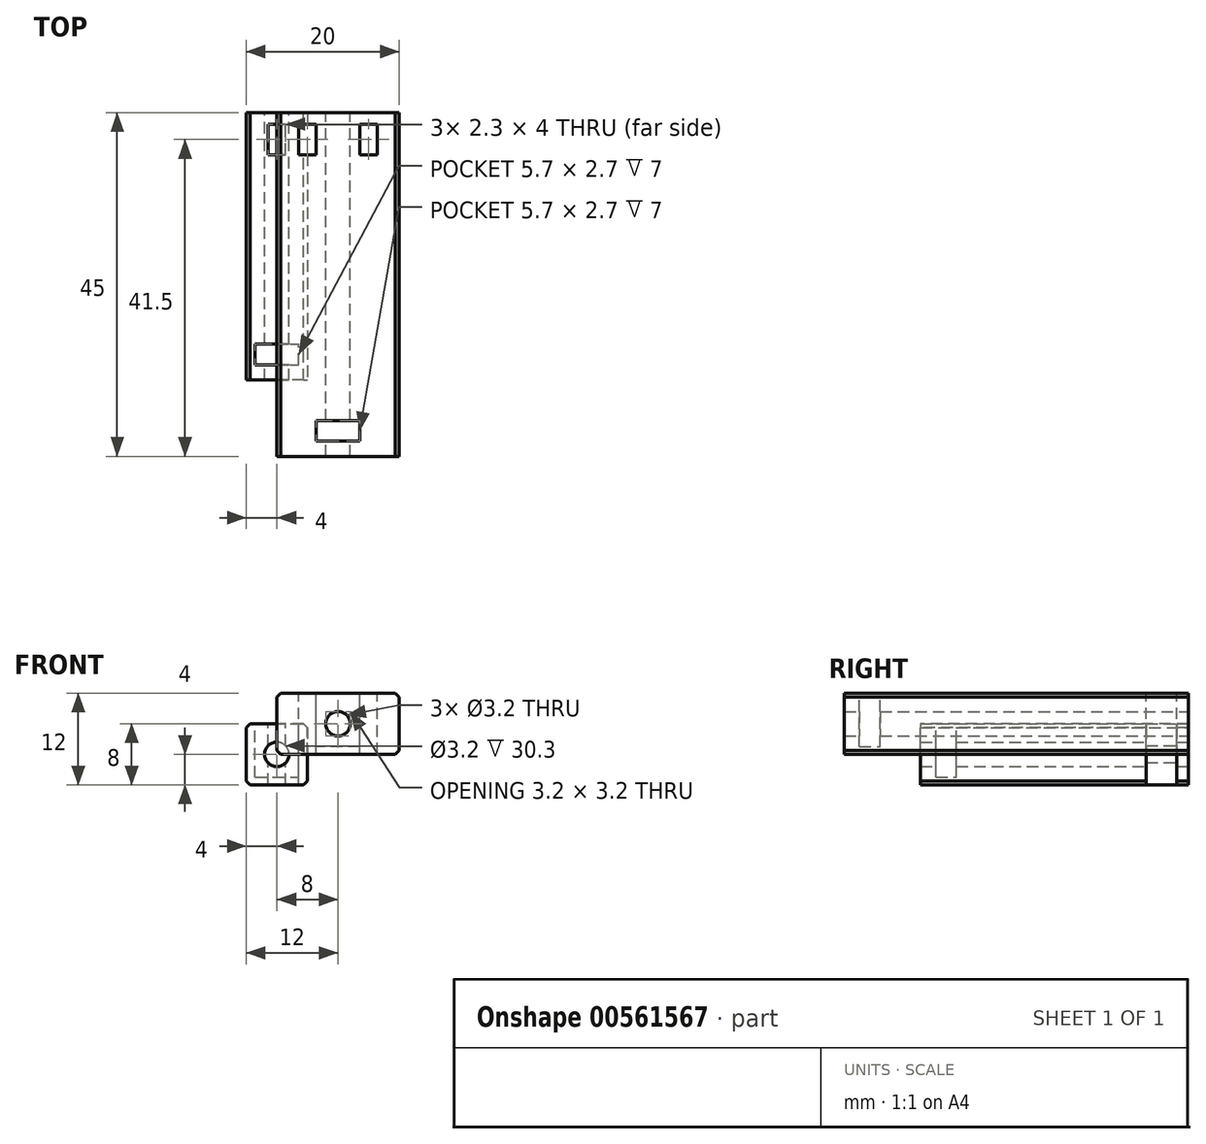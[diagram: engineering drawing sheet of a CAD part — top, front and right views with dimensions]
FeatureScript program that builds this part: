
annotation { "Feature Type Name" : "Feature", "Feature Type Description" : "" }
export const myFeature = defineFeature(function(context is Context, id is Id, definition is map)
    precondition{}
    {
        {
            var Q0;
            Q0=qCreatedBy(makeId("Front.planeOp"),FACE);
            var sketch = newSketch(context, id + "F0", { "sketchPlane" : qUnion([Q0])});
            skLineSegment(sketch, "E0.bottom", {"start": v(4, -4) * mm, "end": v(-4, -4) * mm});
            skLineSegment(sketch, "E0.top", {"start": v(4, 4) * mm, "end": v(-4, 4) * mm});
            skLineSegment(sketch, "E0.left", {"start": v(4, -4) * mm, "end": v(4, 4) * mm});
            skLineSegment(sketch, "E0.right", {"start": v(-4, -4) * mm, "end": v(-4, 4) * mm});
            skPoint(sketch, "E0.middle", {"position": v(0, 0) * mm});
            skCircle(sketch, "E1", {"center": v(0, 0) * mm, "radius": 1.6 * mm});
            skSolve(sketch);
        }
        {
            var Q0;
            Q0=makeQuery(id+"F0.imprint","IMPRINT",FACE,{"disambiguationData":[TD([[makeQuery(id+"F0.imprint","IMPRINT",EDGE,{"derivedFrom":sQuery(id+"F0.wireOp",EDGE,"E0.bottom")}),-1.0]])]});
            extrude(context, id + "F1", {"entities" : qUnion([Q0]), "depth" : 35 * mm});
        }
        {
            var Q0;
            Q0=makeQuery(id+"F1.opExtrude","SWEPT_FACE",FACE,{"disambiguationData":[OSD([sQuery(id+"F0.wireOp",EDGE,"E0.top")])]});
            var sketch = newSketch(context, id + "F2", { "sketchPlane" : qUnion([Q0])});
            skLineSegment(sketch, "E2.bottom", {"start": v(-2.85, -33) * mm, "end": v(2.85, -33) * mm});
            skLineSegment(sketch, "E2.top", {"start": v(-2.85, -30.3) * mm, "end": v(2.85, -30.3) * mm});
            skLineSegment(sketch, "E2.left", {"start": v(-2.85, -33) * mm, "end": v(-2.85, -30.3) * mm});
            skLineSegment(sketch, "E2.right", {"start": v(2.85, -33) * mm, "end": v(2.85, -30.3) * mm});
            skPoint(sketch, "E2.middle", {"position": v(0, -31.65) * mm});
            skSolve(sketch);
        }
        {
            var Q0;
            Q0=makeQuery(id+"F2.imprint","IMPRINT",FACE,{"disambiguationData":[TD([[makeQuery(id+"F2.imprint","IMPRINT",EDGE,{"derivedFrom":sQuery(id+"F2.wireOp",EDGE,"E2.bottom")}),1.0]])]});
            extrude(context, id + "F3", {"entities" : qUnion([Q0]), "operationType" : NewBodyOperationType.REMOVE, "oppositeDirection" : true, "depth" : 7 * mm});
        }
        {
            var Q0;
            Q0=makeQuery(id+"F1.opExtrude","SWEPT_FACE",FACE,{"disambiguationData":[OSD([sQuery(id+"F0.wireOp",EDGE,"E0.top")])]});
            var sketch = newSketch(context, id + "F4", { "sketchPlane" : qUnion([Q0])});
            skLineSegment(sketch, "E3.bottom", {"start": v(-1.15, -5.5) * mm, "end": v(1.15, -5.5) * mm});
            skLineSegment(sketch, "E3.top", {"start": v(-1.15, -1.5) * mm, "end": v(1.15, -1.5) * mm});
            skLineSegment(sketch, "E3.left", {"start": v(-1.15, -5.5) * mm, "end": v(-1.15, -1.5) * mm});
            skLineSegment(sketch, "E3.right", {"start": v(1.15, -5.5) * mm, "end": v(1.15, -1.5) * mm});
            skPoint(sketch, "E3.middle", {"position": v(0, -3.5) * mm});
            skSolve(sketch);
        }
        {
            var Q0;
            Q0=makeQuery(id+"F4.imprint","IMPRINT",FACE,{"disambiguationData":[TD([[makeQuery(id+"F4.imprint","IMPRINT",EDGE,{"derivedFrom":sQuery(id+"F4.wireOp",EDGE,"E3.bottom")}),1.0]])]});
            extrude(context, id + "F5", {"entities" : qUnion([Q0]), "operationType" : NewBodyOperationType.REMOVE, "endBound" : BoundingType.THROUGH_ALL, "oppositeDirection" : true, "depth" : 25 * mm});
        }
        {
            var Q0;
            Q0=makeQuery(id+"F1.opExtrude","SWEPT_EDGE",EDGE,{"disambiguationData":[OSD([sQuery(id+"F0.wireOp",EDGE,"E0.top"),sQuery(id+"F0.wireOp",EDGE,"E0.right")])]});
            var Q1;
            Q1=makeQuery(id+"F1.opExtrude","SWEPT_EDGE",EDGE,{"disambiguationData":[OSD([sQuery(id+"F0.wireOp",EDGE,"E0.top"),sQuery(id+"F0.wireOp",EDGE,"E0.left")])]});
            var Q2;
            Q2=makeQuery(id+"F1.opExtrude","SWEPT_EDGE",EDGE,{"disambiguationData":[OSD([sQuery(id+"F0.wireOp",EDGE,"E0.bottom"),sQuery(id+"F0.wireOp",EDGE,"E0.right")])]});
            var Q3;
            Q3=makeQuery(id+"F1.opExtrude","SWEPT_EDGE",EDGE,{"disambiguationData":[OSD([sQuery(id+"F0.wireOp",EDGE,"E0.bottom"),sQuery(id+"F0.wireOp",EDGE,"E0.left")])]});
            chamfer(context, id + "F6", {"entities" : qUnion([Q0, Q1, Q2, Q3]), "width" : .5 * mm, "tangentPropagation" : true});
        }
        {
            var Q0;
            Q0=qCreatedBy(makeId("Front.planeOp"),FACE);
            var sketch = newSketch(context, id + "F7", { "sketchPlane" : qUnion([Q0])});
            skLineSegment(sketch, "E4.bottom", {"start": v(0, 0) * mm, "end": v(16, 0) * mm});
            skLineSegment(sketch, "E4.top", {"start": v(0, 8) * mm, "end": v(16, 8) * mm});
            skLineSegment(sketch, "E4.left", {"start": v(0, 0) * mm, "end": v(0, 8) * mm});
            skLineSegment(sketch, "E4.right", {"start": v(16, 0) * mm, "end": v(16, 8) * mm});
            skCircle(sketch, "E5", {"center": v(8, 4) * mm, "radius": 1.6 * mm});
            skPoint(sketch, "E5.centerSnap0", {"position": v(8, 8) * mm});
            skLineSegment(sketch, "E6", {"start": v(0, 4) * mm, "end": v(16, 4) * mm, "construction": true});
            skSolve(sketch);
        }
        {
            var Q0;
            Q0=makeQuery(id+"F7.imprint","IMPRINT",FACE,{"disambiguationData":[TD([[makeQuery(id+"F7.imprint","IMPRINT",EDGE,{"derivedFrom":sQuery(id+"F7.wireOp",EDGE,"E4.bottom")}),1.0]])]});
            extrude(context, id + "F8", {"entities" : qUnion([Q0]), "depth" : 45 * mm});
        }
        {
            var Q0;
            Q0=makeQuery(id+"F8.opExtrude","SWEPT_FACE",FACE,{"disambiguationData":[OSD([sQuery(id+"F7.wireOp",EDGE,"E4.top")])]});
            var sketch = newSketch(context, id + "F9", { "sketchPlane" : qUnion([Q0])});
            skLineSegment(sketch, "E7.bottom", {"start": v(10.85, -43) * mm, "end": v(5.15, -43) * mm});
            skLineSegment(sketch, "E7.top", {"start": v(10.85, -40.3) * mm, "end": v(5.15, -40.3) * mm});
            skLineSegment(sketch, "E7.left", {"start": v(10.85, -43) * mm, "end": v(10.85, -40.3) * mm});
            skLineSegment(sketch, "E7.right", {"start": v(5.15, -43) * mm, "end": v(5.15, -40.3) * mm});
            skPoint(sketch, "E7.middle", {"position": v(8, -41.65) * mm});
            skPoint(sketch, "E7.middle.positionSnap0", {"position": v(8, -45) * mm});
            skPoint(sketch, "E7.centerSnap0", {"position": v(8, -45) * mm});
            skSolve(sketch);
        }
        {
            var Q0;
            Q0=qSketchRegion(id+"F9",true);
            extrude(context, id + "F10", {"entities" : qUnion([Q0]), "operationType" : NewBodyOperationType.REMOVE, "oppositeDirection" : true, "depth" : 7 * mm});
        }
        {
            var Q0;
            Q0=makeQuery(id+"F8.opExtrude","SWEPT_EDGE",EDGE,{"disambiguationData":[OSD([sQuery(id+"F7.wireOp",EDGE,"E4.top"),sQuery(id+"F7.wireOp",EDGE,"E4.left")])]});
            var Q1;
            Q1=makeQuery(id+"F8.opExtrude","SWEPT_EDGE",EDGE,{"disambiguationData":[OSD([sQuery(id+"F7.wireOp",EDGE,"E4.top"),sQuery(id+"F7.wireOp",EDGE,"E4.right")])]});
            var Q2;
            Q2=makeQuery(id+"F8.opExtrude","SWEPT_EDGE",EDGE,{"disambiguationData":[OSD([sQuery(id+"F7.wireOp",EDGE,"E4.bottom"),sQuery(id+"F7.wireOp",EDGE,"E4.right")])]});
            var Q3;
            Q3=makeQuery(id+"F8.opExtrude","SWEPT_EDGE",EDGE,{"disambiguationData":[OSD([sQuery(id+"F7.wireOp",EDGE,"E4.bottom"),sQuery(id+"F7.wireOp",EDGE,"E4.left")])]});
            chamfer(context, id + "F11", {"entities" : qUnion([Q0, Q1, Q2, Q3]), "width" : 0.5 * mm, "tangentPropagation" : true});
        }
        {
            var Q0;
            Q0=makeQuery(id+"F8.opExtrude","SWEPT_FACE",FACE,{"disambiguationData":[OSD([sQuery(id+"F7.wireOp",EDGE,"E4.top")])]});
            var sketch = newSketch(context, id + "F12", { "sketchPlane" : qUnion([Q0])});
            skLineSegment(sketch, "E8.bottom", {"start": v(5.15, -5.5) * mm, "end": v(2.85, -5.5) * mm});
            skLineSegment(sketch, "E8.top", {"start": v(5.15, -1.5) * mm, "end": v(2.85, -1.5) * mm});
            skLineSegment(sketch, "E8.left", {"start": v(5.15, -5.5) * mm, "end": v(5.15, -1.5) * mm});
            skLineSegment(sketch, "E8.right", {"start": v(2.85, -5.5) * mm, "end": v(2.85, -1.5) * mm});
            skPoint(sketch, "E8.middle", {"position": v(4, -3.5) * mm});
            skLineSegment(sketch, "E9", {"start": v(8, 0) * mm, "end": v(8, -10.75) * mm, "construction": true});
            skPoint(sketch, "E10.MirrorP", {"position": v(12, -3.5) * mm});
            skLineSegment(sketch, "E11.MirrorCS", {"start": v(13.15, -5.5) * mm, "end": v(13.15, -1.5) * mm});
            skLineSegment(sketch, "E12.MirrorCS", {"start": v(10.85, -5.5) * mm, "end": v(10.85, -1.5) * mm});
            skLineSegment(sketch, "E13.MirrorCS", {"start": v(10.85, -5.5) * mm, "end": v(13.15, -5.5) * mm});
            skLineSegment(sketch, "E14.MirrorCS", {"start": v(10.85, -1.5) * mm, "end": v(13.15, -1.5) * mm});
            skSolve(sketch);
        }
        {
            var Q0;
            Q0=qSketchRegion(id+"F12",true);
            extrude(context, id + "F13", {"entities" : qUnion([Q0]), "operationType" : NewBodyOperationType.REMOVE, "endBound" : BoundingType.THROUGH_ALL, "oppositeDirection" : true, "depth" : 25 * mm});
        }
    });
